# Revit family: IEK_Зажим соединительный параллельный_Пруток-стержень_8-10мм-18мм_Соединение
name_source: partatom
category: Соединительные детали воздуховодов
units: mm (PartAtom-declared; Revit-internal decimal feet)

## family parameters
Всегда вертикально = Да
На основе рабочей плоскости = Нет
Общий = Да
При загрузке вырезать с полостями = Нет
Размер круглого соединителя = Использовать диаметр
Тип детали = Соединение

## types (3) — shared parameters
ADSK_URL страницы изделия = https://www.iek.ru
ADSK_Версия Revit = 2019
ADSK_Версия семейства = 1.0
ADSK_Группирование = VIII. ЭЛЕМЕНТЫ ВНЕШНЕЙ МОЛНИЕЗАЩИТЫ
ADSK_Единица измерения = шт
ADSK_Завод-изготовитель = IEK
IEK_Описание = Универсальная конструкция зажима позволяет использовать его с проводниками различной формы и габаритами.

## per-type parameters (varying)
| type | ADSK_Код изделия | ADSK_Масса | ADSK_Материал | ADSK_Материал наименование | ADSK_Наименование | IEK_URL | IEK_Цена за единицу | KSI_CMa_Строительные материалы |
| 8-10_18_Сталь оцинкованная | ZCC94-11-1-18 | 0.115 | Сталь оцинкованная | Сталь оцинкованная | Зажим соединительный параллельный пруток-стержень оцинкованная сталь IEK | https://www.iek.ru | 357 | 24.10.35.000.08.3.05.06-0001 |
| 8-10_18_Медь | ZCC94-50-1-18 | 0.15 | Медь | Медь | Зажим соед. паралл. пруток-стержень медь IEK | https://www.iek.ru | 1392 | СТ 10 12 20 10 |
| 8-10_18_Латунь | ZCC94-40-1-18 | 0.14 | Латунь | Латунь | Зажим соед. паралл. пруток-стержень латунь IEK |  | 1176 | 10.2.01.02 |
